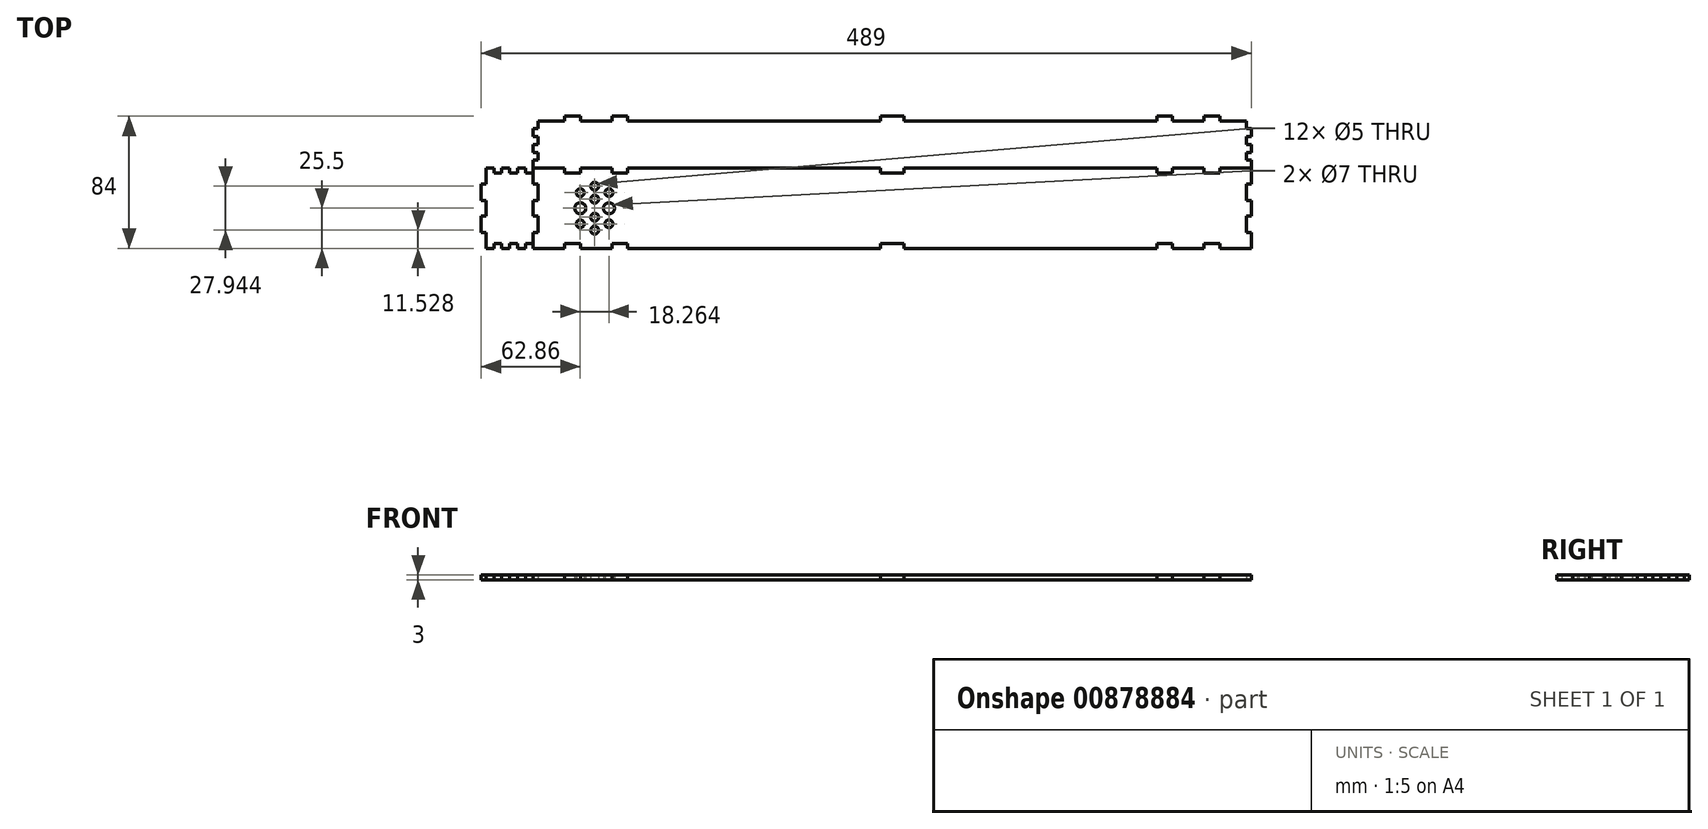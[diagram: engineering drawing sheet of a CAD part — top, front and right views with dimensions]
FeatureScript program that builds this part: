
annotation { "Feature Type Name" : "Feature", "Feature Type Description" : "" }
export const myFeature = defineFeature(function(context is Context, id is Id, definition is map)
    precondition{}
    {
        {
            assignVariable(context, id + "F0", {"name" : "MDF", "anyValue" : 3});
        }
        {
            var Q0;
            Q0=qCreatedBy(makeId("Top.planeOp"),FACE);
            var sketch = newSketch(context, id + "F1", { "sketchPlane" : qUnion([Q0])});
            skLineSegment(sketch, "E0", {"start": v(-228, 25.5) * mm, "end": v(-208, 25.5) * mm});
            skLineSegment(sketch, "E1", {"start": v(228, 25.5) * mm, "end": v(228, 15.5) * mm});
            skLineSegment(sketch, "E2", {"start": v(-228, -25.5) * mm, "end": v(-228, -15.5) * mm});
            skLineSegment(sketch, "E3", {"start": v(-198, 25.5) * mm, "end": v(-178, 25.5) * mm});
            skLineSegment(sketch, "E4", {"start": v(-208, 25.5) * mm, "end": v(-208, 22.5) * mm});
            skLineSegment(sketch, "E5", {"start": v(-208, 22.5) * mm, "end": v(-198, 22.5) * mm});
            skLineSegment(sketch, "E6", {"start": v(-198, 22.5) * mm, "end": v(-198, 25.5) * mm});
            skLineSegment(sketch, "E7.1.0.0", {"start": v(-178, 25.5) * mm, "end": v(-178, 22.5) * mm});
            skLineSegment(sketch, "E7.1.0.2", {"start": v(-168, 22.5) * mm, "end": v(-168, 25.5) * mm});
            skLineSegment(sketch, "E7.2.0.0", {"start": v(-7.5, 25.5) * mm, "end": v(-7.5, 22.5) * mm});
            skLineSegment(sketch, "E8.trimOffspring", {"start": v(-168, 25.5) * mm, "end": v(-7.5, 25.5) * mm});
            skLineSegment(sketch, "E9", {"start": v(-178, 22.5) * mm, "end": v(-168, 22.5) * mm});
            skLineSegment(sketch, "E10.MirrorCS", {"start": v(208, 25.5) * mm, "end": v(208, 22.5) * mm});
            skLineSegment(sketch, "E11.MirrorCS", {"start": v(198, 22.5) * mm, "end": v(198, 25.5) * mm});
            skLineSegment(sketch, "E12.MirrorCS", {"start": v(198, 25.5) * mm, "end": v(178, 25.5) * mm});
            skLineSegment(sketch, "E13.MirrorCS", {"start": v(178, 25.5) * mm, "end": v(178, 22.5) * mm});
            skLineSegment(sketch, "E14.MirrorCS", {"start": v(168, 22.5) * mm, "end": v(168, 25.5) * mm});
            skLineSegment(sketch, "E15.MirrorCS", {"start": v(168, 25.5) * mm, "end": v(7.5, 25.5) * mm});
            skLineSegment(sketch, "E16.MirrorCS", {"start": v(7.5, 25.5) * mm, "end": v(7.5, 22.5) * mm});
            skLineSegment(sketch, "E17", {"start": v(-7.5, 22.5) * mm, "end": v(7.5, 22.5) * mm});
            skLineSegment(sketch, "E18", {"start": v(168, 22.5) * mm, "end": v(178, 22.5) * mm});
            skLineSegment(sketch, "E19", {"start": v(198, 22.5) * mm, "end": v(208, 22.5) * mm});
            skLineSegment(sketch, "E20", {"start": v(-90, 40.5) * mm, "end": v(148.24, 40.5) * mm, "construction": true});
            skLineSegment(sketch, "E21", {"start": v(-228, 15.5) * mm, "end": v(-225, 15.5) * mm});
            skLineSegment(sketch, "E22", {"start": v(-225, 15.5) * mm, "end": v(-225, 5) * mm});
            skLineSegment(sketch, "E23", {"start": v(-225, -5) * mm, "end": v(-228, -5) * mm});
            skLineSegment(sketch, "E24.MirrorCS", {"start": v(-228, -15.5) * mm, "end": v(-225, -15.5) * mm});
            skLineSegment(sketch, "E25.MirrorCS", {"start": v(-225, -15.5) * mm, "end": v(-225, -5) * mm});
            skLineSegment(sketch, "E26.MirrorCS", {"start": v(-225, 5) * mm, "end": v(-228, 5) * mm});
            skLineSegment(sketch, "E27.trimOffspring", {"start": v(-228, -5) * mm, "end": v(-228, 5) * mm});
            skLineSegment(sketch, "E28.MirrorCS", {"start": v(225, -5) * mm, "end": v(228, -5) * mm});
            skLineSegment(sketch, "E29.MirrorCS", {"start": v(228, 15.5) * mm, "end": v(225, 15.5) * mm});
            skLineSegment(sketch, "E30.MirrorCS", {"start": v(225, 5) * mm, "end": v(228, 5) * mm});
            skLineSegment(sketch, "E31.MirrorCS", {"start": v(228, -15.5) * mm, "end": v(225, -15.5) * mm});
            skLineSegment(sketch, "E32.trimOffspring", {"start": v(228, 5) * mm, "end": v(228, -5) * mm});
            skLineSegment(sketch, "E33.trimOffspring", {"start": v(228, -15.5) * mm, "end": v(228, -25.5) * mm});
            skLineSegment(sketch, "E34.MirrorCS", {"start": v(-208, -22.5) * mm, "end": v(-198, -22.5) * mm});
            skLineSegment(sketch, "E35.MirrorCS", {"start": v(-178, -22.5) * mm, "end": v(-168, -22.5) * mm});
            skLineSegment(sketch, "E36.MirrorCS", {"start": v(-7.5, -22.5) * mm, "end": v(7.5, -22.5) * mm});
            skLineSegment(sketch, "E37.MirrorCS", {"start": v(168, -22.5) * mm, "end": v(178, -22.5) * mm});
            skLineSegment(sketch, "E38.MirrorCS", {"start": v(198, -22.5) * mm, "end": v(208, -22.5) * mm});
            skLineSegment(sketch, "E39.MirrorCS", {"start": v(-208, -25.5) * mm, "end": v(-208, -22.5) * mm});
            skLineSegment(sketch, "E40.MirrorCS", {"start": v(-198, -22.5) * mm, "end": v(-198, -25.5) * mm});
            skLineSegment(sketch, "E41.MirrorCS", {"start": v(-178, -25.5) * mm, "end": v(-178, -22.5) * mm});
            skLineSegment(sketch, "E42.MirrorCS", {"start": v(-168, -22.5) * mm, "end": v(-168, -25.5) * mm});
            skLineSegment(sketch, "E43.MirrorCS", {"start": v(-7.5, -25.5) * mm, "end": v(-7.5, -22.5) * mm});
            skLineSegment(sketch, "E44.MirrorCS", {"start": v(7.5, -25.5) * mm, "end": v(7.5, -22.5) * mm});
            skLineSegment(sketch, "E45.MirrorCS", {"start": v(168, -22.5) * mm, "end": v(168, -25.5) * mm});
            skLineSegment(sketch, "E46.MirrorCS", {"start": v(178, -25.5) * mm, "end": v(178, -22.5) * mm});
            skLineSegment(sketch, "E47.MirrorCS", {"start": v(198, -22.5) * mm, "end": v(198, -25.5) * mm});
            skLineSegment(sketch, "E48.MirrorCS", {"start": v(208, -25.5) * mm, "end": v(208, -22.5) * mm});
            skLineSegment(sketch, "E49.trimOffspring", {"start": v(-208, -25.5) * mm, "end": v(-228, -25.5) * mm});
            skLineSegment(sketch, "E50.trimOffspring", {"start": v(-178, -25.5) * mm, "end": v(-198, -25.5) * mm});
            skLineSegment(sketch, "E51.trimOffspring", {"start": v(-7.5, -25.5) * mm, "end": v(-168, -25.5) * mm});
            skLineSegment(sketch, "E52.trimOffspring", {"start": v(168, -25.5) * mm, "end": v(7.5, -25.5) * mm});
            skLineSegment(sketch, "E53.trimOffspring", {"start": v(198, -25.5) * mm, "end": v(178, -25.5) * mm});
            skLineSegment(sketch, "E54", {"start": v(208, 25.5) * mm, "end": v(228, 25.5) * mm});
            skLineSegment(sketch, "E55", {"start": v(-228, 15.5) * mm, "end": v(-228, 25.5) * mm});
            skLineSegment(sketch, "E56", {"start": v(208, -25.5) * mm, "end": v(228, -25.5) * mm});
            skLineSegment(sketch, "E57", {"start": v(-228, 25.5) * mm, "end": v(-307.39, 109.63) * mm, "construction": true});
            skLineSegment(sketch, "E58", {"start": v(-228, 25.5) * mm, "end": v(-74.23, 179.27) * mm, "construction": true});
            skLineSegment(sketch, "E59.MirrorCS", {"start": v(-228, 25.5) * mm, "end": v(-228, 30.5) * mm});
            skLineSegment(sketch, "E60.MirrorCS", {"start": v(-225, 55.5) * mm, "end": v(-208, 55.5) * mm});
            skLineSegment(sketch, "E61.MirrorCS", {"start": v(-208, 55.5) * mm, "end": v(-208, 58.5) * mm});
            skLineSegment(sketch, "E62.MirrorCS", {"start": v(-208, 58.5) * mm, "end": v(-198, 58.5) * mm});
            skLineSegment(sketch, "E63.MirrorCS", {"start": v(-198, 58.5) * mm, "end": v(-198, 55.5) * mm});
            skLineSegment(sketch, "E64.MirrorCS", {"start": v(-198, 55.5) * mm, "end": v(-178, 55.5) * mm});
            skLineSegment(sketch, "E65.MirrorCS", {"start": v(-178, 55.5) * mm, "end": v(-178, 58.5) * mm});
            skLineSegment(sketch, "E66.MirrorCS", {"start": v(-178, 58.5) * mm, "end": v(-168, 58.5) * mm});
            skLineSegment(sketch, "E67.MirrorCS", {"start": v(-168, 58.5) * mm, "end": v(-168, 55.5) * mm});
            skLineSegment(sketch, "E68.MirrorCS", {"start": v(-168, 55.5) * mm, "end": v(-7.5, 55.5) * mm});
            skLineSegment(sketch, "E69.MirrorCS", {"start": v(-7.5, 55.5) * mm, "end": v(-7.5, 58.5) * mm});
            skLineSegment(sketch, "E70.MirrorCS", {"start": v(-7.5, 58.5) * mm, "end": v(7.5, 58.5) * mm});
            skLineSegment(sketch, "E71.MirrorCS", {"start": v(7.5, 55.5) * mm, "end": v(7.5, 58.5) * mm});
            skLineSegment(sketch, "E72.MirrorCS", {"start": v(168, 55.5) * mm, "end": v(7.5, 55.5) * mm});
            skLineSegment(sketch, "E73.MirrorCS", {"start": v(168, 58.5) * mm, "end": v(168, 55.5) * mm});
            skLineSegment(sketch, "E74.MirrorCS", {"start": v(168, 58.5) * mm, "end": v(178, 58.5) * mm});
            skLineSegment(sketch, "E75.MirrorCS", {"start": v(178, 55.5) * mm, "end": v(178, 58.5) * mm});
            skLineSegment(sketch, "E76.MirrorCS", {"start": v(198, 55.5) * mm, "end": v(178, 55.5) * mm});
            skLineSegment(sketch, "E77.MirrorCS", {"start": v(198, 58.5) * mm, "end": v(198, 55.5) * mm});
            skLineSegment(sketch, "E78.MirrorCS", {"start": v(198, 58.5) * mm, "end": v(208, 58.5) * mm});
            skLineSegment(sketch, "E79.MirrorCS", {"start": v(208, 55.5) * mm, "end": v(208, 58.5) * mm});
            skLineSegment(sketch, "E80.MirrorCS", {"start": v(208, 55.5) * mm, "end": v(228, 55.5) * mm});
            skLineSegment(sketch, "E81.MirrorCS", {"start": v(228, -111.4) * mm, "end": v(225, -111.4) * mm});
            skLineSegment(sketch, "E82.MirrorCS", {"start": v(225, -121.4) * mm, "end": v(225, -111.4) * mm});
            skLineSegment(sketch, "E83.MirrorCS", {"start": v(228, -121.4) * mm, "end": v(225, -121.4) * mm});
            skLineSegment(sketch, "E84.MirrorCS", {"start": v(228, -142.55) * mm, "end": v(228, -121.4) * mm});
            skLineSegment(sketch, "E85.MirrorCS", {"start": v(228, -142.55) * mm, "end": v(225, -142.55) * mm});
            skLineSegment(sketch, "E86", {"start": v(228, 50.5) * mm, "end": v(228, 45.5) * mm});
            skPoint(sketch, "E87.orphan", {"position": v(-228, 147.7) * mm});
            skLineSegment(sketch, "E88", {"start": v(65.44, -22.5) * mm, "end": v(-228, -22.5) * mm, "construction": true});
            skLineSegment(sketch, "E89", {"start": v(225, 15.5) * mm, "end": v(225, 5) * mm});
            skLineSegment(sketch, "E90", {"start": v(225, -5) * mm, "end": v(225, -15.5) * mm});
            skLineSegment(sketch, "E91", {"start": v(-228, 22.5) * mm, "end": v(-233, 22.5) * mm});
            skLineSegment(sketch, "E92", {"start": v(-233, 22.5) * mm, "end": v(-233, 25.5) * mm});
            skLineSegment(sketch, "E93", {"start": v(-233, 25.5) * mm, "end": v(-238, 25.5) * mm});
            skLineSegment(sketch, "E94", {"start": v(-238, 25.5) * mm, "end": v(-238, 22.5) * mm});
            skLineSegment(sketch, "E95", {"start": v(-238, 22.5) * mm, "end": v(-243, 22.5) * mm});
            skLineSegment(sketch, "E96", {"start": v(-243, 22.5) * mm, "end": v(-243, 25.5) * mm});
            skLineSegment(sketch, "E97", {"start": v(-243, 25.5) * mm, "end": v(-248, 25.5) * mm});
            skLineSegment(sketch, "E98", {"start": v(-248, 25.5) * mm, "end": v(-248, 22.5) * mm});
            skPoint(sketch, "E98.endSnap0", {"position": v(-240.5, 22.5) * mm});
            skLineSegment(sketch, "E99", {"start": v(-248, 22.5) * mm, "end": v(-253, 22.5) * mm});
            skLineSegment(sketch, "E100", {"start": v(-253, 22.5) * mm, "end": v(-253, 25.5) * mm});
            skLineSegment(sketch, "E101", {"start": v(-253, 25.5) * mm, "end": v(-258, 25.5) * mm});
            skLineSegment(sketch, "E102", {"start": v(-258, 25.5) * mm, "end": v(-258, 15.5) * mm});
            skLineSegment(sketch, "E103", {"start": v(-255.3, 0) * mm, "end": v(-174.46, 0) * mm, "construction": true});
            skLineSegment(sketch, "E104.MirrorCS", {"start": v(-258, -25.5) * mm, "end": v(-258, -15.5) * mm});
            skLineSegment(sketch, "E105.MirrorCS", {"start": v(-253, -25.5) * mm, "end": v(-258, -25.5) * mm});
            skLineSegment(sketch, "E106.MirrorCS", {"start": v(-253, -22.5) * mm, "end": v(-253, -25.5) * mm});
            skLineSegment(sketch, "E107.MirrorCS", {"start": v(-248, -22.5) * mm, "end": v(-253, -22.5) * mm});
            skLineSegment(sketch, "E108.MirrorCS", {"start": v(-248, -25.5) * mm, "end": v(-248, -22.5) * mm});
            skLineSegment(sketch, "E109.MirrorCS", {"start": v(-243, -25.5) * mm, "end": v(-248, -25.5) * mm});
            skLineSegment(sketch, "E110.MirrorCS", {"start": v(-243, -22.5) * mm, "end": v(-243, -25.5) * mm});
            skLineSegment(sketch, "E111.MirrorCS", {"start": v(-238, -22.5) * mm, "end": v(-243, -22.5) * mm});
            skLineSegment(sketch, "E112.MirrorCS", {"start": v(-238, -25.5) * mm, "end": v(-238, -22.5) * mm});
            skLineSegment(sketch, "E113.MirrorCS", {"start": v(-233, -25.5) * mm, "end": v(-238, -25.5) * mm});
            skLineSegment(sketch, "E114.MirrorCS", {"start": v(-233, -22.5) * mm, "end": v(-233, -25.5) * mm});
            skLineSegment(sketch, "E115.MirrorCS", {"start": v(-228, -22.5) * mm, "end": v(-233, -22.5) * mm});
            skLineSegment(sketch, "E116", {"start": v(-258, 15.5) * mm, "end": v(-261, 15.5) * mm});
            skLineSegment(sketch, "E117", {"start": v(-261, 15.5) * mm, "end": v(-261, 5) * mm});
            skLineSegment(sketch, "E118", {"start": v(-261, 5) * mm, "end": v(-258, 5) * mm});
            skLineSegment(sketch, "E119", {"start": v(-258, 5) * mm, "end": v(-258, -5) * mm});
            skLineSegment(sketch, "E120", {"start": v(-258, -5) * mm, "end": v(-261, -5) * mm});
            skLineSegment(sketch, "E121", {"start": v(-261, -5) * mm, "end": v(-261, -15.5) * mm});
            skLineSegment(sketch, "E122", {"start": v(-261, -15.5) * mm, "end": v(-258, -15.5) * mm});
            skLineSegment(sketch, "E123.trimOffspring", {"start": v(-258, 5) * mm, "end": v(-258, 0) * mm});
            skLineSegment(sketch, "E124.trimOffspring", {"start": v(-258, -5) * mm, "end": v(-258, 0) * mm});
            skLineSegment(sketch, "E125", {"start": v(-228, 30.5) * mm, "end": v(-225, 30.5) * mm});
            skLineSegment(sketch, "E126", {"start": v(-225, 30.5) * mm, "end": v(-225, 35.5) * mm});
            skLineSegment(sketch, "E127", {"start": v(-225, 35.5) * mm, "end": v(-228, 35.5) * mm});
            skLineSegment(sketch, "E128", {"start": v(-228, 40.5) * mm, "end": v(-225, 40.5) * mm});
            skLineSegment(sketch, "E129", {"start": v(-225, 40.5) * mm, "end": v(-225, 45.5) * mm});
            skLineSegment(sketch, "E130", {"start": v(-225, 45.5) * mm, "end": v(-228, 45.5) * mm});
            skLineSegment(sketch, "E131", {"start": v(-225, 50.5) * mm, "end": v(-225, 55.5) * mm});
            skLineSegment(sketch, "E132.trimOffspring", {"start": v(-228, 35.5) * mm, "end": v(-228, 40.5) * mm});
            skLineSegment(sketch, "E133.trimOffspring", {"start": v(-228, 45.5) * mm, "end": v(-228, 50.5) * mm});
            skLineSegment(sketch, "E134", {"start": v(-228, 50.5) * mm, "end": v(-225, 50.5) * mm});
            skLineSegment(sketch, "E135", {"start": v(0, 0) * mm, "end": v(0, 93.3) * mm, "construction": true});
            skLineSegment(sketch, "E136.MirrorCS", {"start": v(225, 50.5) * mm, "end": v(225, 55.5) * mm});
            skLineSegment(sketch, "E137.MirrorCS", {"start": v(228, 50.5) * mm, "end": v(225, 50.5) * mm});
            skLineSegment(sketch, "E138.MirrorCS", {"start": v(228, 45.5) * mm, "end": v(228, 50.5) * mm});
            skLineSegment(sketch, "E139.MirrorCS", {"start": v(225, 45.5) * mm, "end": v(228, 45.5) * mm});
            skLineSegment(sketch, "E140.MirrorCS", {"start": v(225, 40.5) * mm, "end": v(225, 45.5) * mm});
            skLineSegment(sketch, "E141.MirrorCS", {"start": v(228, 40.5) * mm, "end": v(225, 40.5) * mm});
            skLineSegment(sketch, "E142.MirrorCS", {"start": v(228, 35.5) * mm, "end": v(228, 40.5) * mm});
            skLineSegment(sketch, "E143.MirrorCS", {"start": v(225, 35.5) * mm, "end": v(228, 35.5) * mm});
            skLineSegment(sketch, "E144.MirrorCS", {"start": v(225, 30.5) * mm, "end": v(225, 35.5) * mm});
            skLineSegment(sketch, "E145.MirrorCS", {"start": v(228, 30.5) * mm, "end": v(225, 30.5) * mm});
            skLineSegment(sketch, "E146.MirrorCS", {"start": v(228, 25.5) * mm, "end": v(228, 30.5) * mm});
            skLineSegment(sketch, "E147.trimOffspring", {"start": v(228, 30.5) * mm, "end": v(228, 25.5) * mm});
            skLineSegment(sketch, "E148.trimOffspring", {"start": v(228, 40.5) * mm, "end": v(228, 35.5) * mm});
            skCircle(sketch, "E149", {"center": v(-198.14, 9.9) * mm, "radius": 2.5 * mm});
            skCircle(sketch, "E150", {"center": v(-189.01, 13.97) * mm, "radius": 2.5 * mm});
            skCircle(sketch, "E151", {"center": v(-179.88, 9.9) * mm, "radius": 2.5 * mm});
            skCircle(sketch, "E152", {"center": v(-189.01, 5.7) * mm, "radius": 2.5 * mm});
            skCircle(sketch, "E153.MirrorC", {"center": v(-179.88, -9.9) * mm, "radius": 2.5 * mm});
            skCircle(sketch, "E154.MirrorC", {"center": v(-189.01, -5.7) * mm, "radius": 2.5 * mm});
            skCircle(sketch, "E155.MirrorC", {"center": v(-189.01, -13.97) * mm, "radius": 2.5 * mm});
            skCircle(sketch, "E156.MirrorC", {"center": v(-198.14, -9.9) * mm, "radius": 2.5 * mm});
            skCircle(sketch, "E157", {"center": v(-198.14, 0) * mm, "radius": 3.5 * mm});
            skCircle(sketch, "E158", {"center": v(-179.88, 0) * mm, "radius": 3.5 * mm});
            skSolve(sketch);
        }
        {
            var Q0;
            {var subQ4=sQuery(id+"F1.wireOp",EDGE,"E21");Q0=makeQuery(id+"F1.imprint","IMPRINT",FACE,{"disambiguationData":[TD([[makeQuery(id+"F1.imprint","IMPRINT",EDGE,{"derivedFrom":subQ4}),-1.0]])]});}
            var Q1;
            {var subQ0=sQuery(id+"F1.wireOp",EDGE,"rbGXvyEr-rcJ9-qHWQ-iufH-F8PwVDv6k9id");Q1=makeQuery(id+"F1.imprint","IMPRINT",FACE,{"disambiguationData":[TD([[makeQuery(id+"F1.imprint","IMPRINT",EDGE,{"derivedFrom":subQ0}),-1.0]])]});}
            var Q2;
            {var subQ4=sQuery(id+"F1.wireOp",EDGE,"E21");Q2=makeQuery(id+"F1.imprint","IMPRINT",FACE,{"disambiguationData":[TD([[makeQuery(id+"F1.imprint","IMPRINT",EDGE,{"derivedFrom":subQ4}),-1.0]])]});}
            var Q3;
            {var subQ0=sQuery(id+"F1.wireOp",EDGE,"GfZ24xhA-2xWa-IL8O-etRM-yisPiMKkurjO");Q3=makeQuery(id+"F1.imprint","IMPRINT",FACE,{"disambiguationData":[TD([[makeQuery(id+"F1.imprint","IMPRINT",EDGE,{"derivedFrom":subQ0}),-1.0]])]});}
            extrude(context, id + "F2", {"entities" : qUnion([Q0, Q1, Q2, Q3]), "depth" : (getVariable(context, 'MDF')) * mm, "offsetDistance" : 25 * mm});
        }
        {
            var Q0;
            {var subQ2=sQuery(id+"F1.wireOp",EDGE,"E0");Q0=makeQuery(id+"F1.imprint","IMPRINT",FACE,{"disambiguationData":[TD([[makeQuery(id+"F1.imprint","IMPRINT",EDGE,{"derivedFrom":subQ2}),-1.0]])]});}
            var Q1;
            {var subQ0=sQuery(id+"F1.wireOp",EDGE,"rbGXvyEr-rcJ9-qHWQ-iufH-F8PwVDv6k9id");Q1=makeQuery(id+"F1.imprint","IMPRINT",FACE,{"disambiguationData":[TD([[makeQuery(id+"F1.imprint","IMPRINT",EDGE,{"derivedFrom":subQ0}),-1.0]])]});}
            var Q2;
            {var subQ0=sQuery(id+"F1.wireOp",EDGE,"YcIgSpRp-awep-ehTJ-AOBv-wXQJOqJfKg8G");Q2=makeQuery(id+"F1.imprint","IMPRINT",FACE,{"disambiguationData":[TD([[makeQuery(id+"F1.imprint","IMPRINT",EDGE,{"derivedFrom":subQ0}),-1.0]])]});}
            var Q3;
            {var subQ4=sQuery(id+"F1.wireOp",EDGE,"E21");Q3=makeQuery(id+"F1.imprint","IMPRINT",FACE,{"disambiguationData":[TD([[makeQuery(id+"F1.imprint","IMPRINT",EDGE,{"derivedFrom":subQ4}),-1.0]])]});}
            var Q4;
            {var subQ0=sQuery(id+"F1.wireOp",EDGE,"GfZ24xhA-2xWa-IL8O-etRM-yisPiMKkurjO");Q4=makeQuery(id+"F1.imprint","IMPRINT",FACE,{"disambiguationData":[TD([[makeQuery(id+"F1.imprint","IMPRINT",EDGE,{"derivedFrom":subQ0}),-1.0]])]});}
            var Q5;
            {var subQ0=sQuery(id+"F1.wireOp",EDGE,"T6HoQtfU-LjOd-NWtG-YFmk-kXrqQ6T8l042");Q5=makeQuery(id+"F1.imprint","IMPRINT",FACE,{"disambiguationData":[TD([[makeQuery(id+"F1.imprint","IMPRINT",EDGE,{"derivedFrom":subQ0}),-1.0]])]});}
            var Q6;
            Q6=makeQuery(id+"F1.imprint","IMPRINT",FACE,{"disambiguationData":[TD([[makeQuery(id+"F1.imprint","IMPRINT",EDGE,{"derivedFrom":sQuery(id+"F1.wireOp",EDGE,"E1")}),1.0]])]});
            var Q7;
            Q7=makeQuery(id+"F1.imprint","IMPRINT",FACE,{"disambiguationData":[TD([[makeQuery(id+"F1.imprint","IMPRINT",EDGE,{"derivedFrom":sQuery(id+"F1.wireOp",EDGE,"E32.trimOffspring")}),1.0]])]});
            var Q8;
            {var subQ1=sQuery(id+"F1.wireOp",EDGE,"E33.trimOffspring");Q8=makeQuery(id+"F1.imprint","IMPRINT",FACE,{"disambiguationData":[TD([[makeQuery(id+"F1.imprint","IMPRINT",EDGE,{"derivedFrom":subQ1}),1.0]])]});}
            var Q9;
            Q9=makeQuery(id+"F1.imprint","IMPRINT",FACE,{"disambiguationData":[TD([[makeQuery(id+"F1.imprint","IMPRINT",EDGE,{"derivedFrom":sQuery(id+"F1.wireOp",EDGE,"NR7x9NeR-g1uV-OuWE-nqgm-Qy7388QoDPan")}),1.0]])]});
            var Q10;
            Q10=makeQuery(id+"F1.imprint","IMPRINT",FACE,{"disambiguationData":[TD([[makeQuery(id+"F1.imprint","IMPRINT",EDGE,{"derivedFrom":sQuery(id+"F1.wireOp",EDGE,"OMaXj8xA-5qEw-IC3M-FVCK-IZFmudWBQMBu")}),1.0]])]});
            extrude(context, id + "F3", {"entities" : qUnion([Q0, Q1, Q2, Q3, Q4, Q5, Q6, Q7, Q8, Q9, Q10]), "depth" : (getVariable(context, 'MDF')) * mm, "offsetDistance" : 25 * mm});
        }
        {
            var Q0;
            {var subQ2=sQuery(id+"F1.wireOp",EDGE,"E0");Q0=makeQuery(id+"F1.imprint","IMPRINT",FACE,{"disambiguationData":[TD([[makeQuery(id+"F1.imprint","IMPRINT",EDGE,{"derivedFrom":subQ2}),-1.0]])]});}
            extrude(context, id + "F4", {"entities" : qUnion([Q0]), "depth" : (getVariable(context, 'MDF')) * mm, "offsetDistance" : 25 * mm});
        }
        {
            var Q0;
            Q0=makeQuery(id+"F1.imprint","IMPRINT",FACE,{"disambiguationData":[TD([[makeQuery(id+"F1.imprint","IMPRINT",EDGE,{"derivedFrom":sQuery(id+"F1.wireOp",EDGE,"E0")}),1.0]])]});
            extrude(context, id + "F5", {"entities" : qUnion([Q0]), "depth" : (getVariable(context, 'MDF')) * mm, "offsetDistance" : 25 * mm});
        }
        {
            var Q0;
            {var subQ4=sQuery(id+"F1.wireOp",EDGE,"E21");Q0=makeQuery(id+"F1.imprint","IMPRINT",FACE,{"disambiguationData":[TD([[makeQuery(id+"F1.imprint","IMPRINT",EDGE,{"derivedFrom":subQ4}),-1.0]])]});}
            extrude(context, id + "F6", {"entities" : qUnion([Q0]), "depth" : (getVariable(context, 'MDF')) * mm, "offsetDistance" : 25 * mm});
        }
        {
            var Q0;
            Q0=makeQuery(id+"F2.opExtrude","SWEPT_BODY",BODY,{"disambiguationData":[OSD([sQuery(id+"F1.wireOp",EDGE,"E2"),sQuery(id+"F1.wireOp",EDGE,"E21"),sQuery(id+"F1.wireOp",EDGE,"E22"),sQuery(id+"F1.wireOp",EDGE,"E23"),sQuery(id+"F1.wireOp",EDGE,"E24.MirrorCS"),sQuery(id+"F1.wireOp",EDGE,"E25.MirrorCS"),sQuery(id+"F1.wireOp",EDGE,"E26.MirrorCS"),sQuery(id+"F1.wireOp",EDGE,"E27.trimOffspring"),sQuery(id+"F1.wireOp",EDGE,"E55"),sQuery(id+"F1.wireOp",EDGE,"E91"),sQuery(id+"F1.wireOp",EDGE,"E92"),sQuery(id+"F1.wireOp",EDGE,"E93"),sQuery(id+"F1.wireOp",EDGE,"E94"),sQuery(id+"F1.wireOp",EDGE,"E95"),sQuery(id+"F1.wireOp",EDGE,"E96"),sQuery(id+"F1.wireOp",EDGE,"E97"),sQuery(id+"F1.wireOp",EDGE,"E98"),sQuery(id+"F1.wireOp",EDGE,"E99"),sQuery(id+"F1.wireOp",EDGE,"E100"),sQuery(id+"F1.wireOp",EDGE,"E101"),sQuery(id+"F1.wireOp",EDGE,"E102"),sQuery(id+"F1.wireOp",EDGE,"E104.MirrorCS"),sQuery(id+"F1.wireOp",EDGE,"E105.MirrorCS"),sQuery(id+"F1.wireOp",EDGE,"E106.MirrorCS"),sQuery(id+"F1.wireOp",EDGE,"E107.MirrorCS"),sQuery(id+"F1.wireOp",EDGE,"E108.MirrorCS"),sQuery(id+"F1.wireOp",EDGE,"E109.MirrorCS"),sQuery(id+"F1.wireOp",EDGE,"E110.MirrorCS"),sQuery(id+"F1.wireOp",EDGE,"E111.MirrorCS"),sQuery(id+"F1.wireOp",EDGE,"E112.MirrorCS"),sQuery(id+"F1.wireOp",EDGE,"E113.MirrorCS"),sQuery(id+"F1.wireOp",EDGE,"E114.MirrorCS"),sQuery(id+"F1.wireOp",EDGE,"E115.MirrorCS"),sQuery(id+"F1.wireOp",EDGE,"E116"),sQuery(id+"F1.wireOp",EDGE,"E117"),sQuery(id+"F1.wireOp",EDGE,"E118"),sQuery(id+"F1.wireOp",EDGE,"E119"),sQuery(id+"F1.wireOp",EDGE,"E120"),sQuery(id+"F1.wireOp",EDGE,"E121"),sQuery(id+"F1.wireOp",EDGE,"E122")])]});
            deleteBodies(context, id + "F7", {"entities" : qUnion([Q0])});
        }
        {
            var Q0;
            Q0=makeQuery(id+"F3.opExtrude","SWEPT_BODY",BODY,{"disambiguationData":[OSD([sQuery(id+"F1.wireOp",EDGE,"E0"),sQuery(id+"F1.wireOp",EDGE,"E1"),sQuery(id+"F1.wireOp",EDGE,"E2"),sQuery(id+"F1.wireOp",EDGE,"E3"),sQuery(id+"F1.wireOp",EDGE,"E4"),sQuery(id+"F1.wireOp",EDGE,"E5"),sQuery(id+"F1.wireOp",EDGE,"E6"),sQuery(id+"F1.wireOp",EDGE,"E7.1.0.0"),sQuery(id+"F1.wireOp",EDGE,"E7.1.0.2"),sQuery(id+"F1.wireOp",EDGE,"E7.2.0.0"),sQuery(id+"F1.wireOp",EDGE,"E8.trimOffspring"),sQuery(id+"F1.wireOp",EDGE,"E9"),sQuery(id+"F1.wireOp",EDGE,"E10.MirrorCS"),sQuery(id+"F1.wireOp",EDGE,"E11.MirrorCS"),sQuery(id+"F1.wireOp",EDGE,"E12.MirrorCS"),sQuery(id+"F1.wireOp",EDGE,"E13.MirrorCS"),sQuery(id+"F1.wireOp",EDGE,"E14.MirrorCS"),sQuery(id+"F1.wireOp",EDGE,"E15.MirrorCS"),sQuery(id+"F1.wireOp",EDGE,"E16.MirrorCS"),sQuery(id+"F1.wireOp",EDGE,"E17"),sQuery(id+"F1.wireOp",EDGE,"E18"),sQuery(id+"F1.wireOp",EDGE,"E19"),sQuery(id+"F1.wireOp",EDGE,"E28.MirrorCS"),sQuery(id+"F1.wireOp",EDGE,"E29.MirrorCS"),sQuery(id+"F1.wireOp",EDGE,"E30.MirrorCS"),sQuery(id+"F1.wireOp",EDGE,"E31.MirrorCS"),sQuery(id+"F1.wireOp",EDGE,"E32.trimOffspring"),sQuery(id+"F1.wireOp",EDGE,"E33.trimOffspring"),sQuery(id+"F1.wireOp",EDGE,"E34.MirrorCS"),sQuery(id+"F1.wireOp",EDGE,"E35.MirrorCS"),sQuery(id+"F1.wireOp",EDGE,"E36.MirrorCS"),sQuery(id+"F1.wireOp",EDGE,"E37.MirrorCS"),sQuery(id+"F1.wireOp",EDGE,"E38.MirrorCS"),sQuery(id+"F1.wireOp",EDGE,"E39.MirrorCS"),sQuery(id+"F1.wireOp",EDGE,"E40.MirrorCS"),sQuery(id+"F1.wireOp",EDGE,"E41.MirrorCS"),sQuery(id+"F1.wireOp",EDGE,"E42.MirrorCS"),sQuery(id+"F1.wireOp",EDGE,"E43.MirrorCS"),sQuery(id+"F1.wireOp",EDGE,"E44.MirrorCS"),sQuery(id+"F1.wireOp",EDGE,"E45.MirrorCS"),sQuery(id+"F1.wireOp",EDGE,"E46.MirrorCS"),sQuery(id+"F1.wireOp",EDGE,"E47.MirrorCS"),sQuery(id+"F1.wireOp",EDGE,"E48.MirrorCS"),sQuery(id+"F1.wireOp",EDGE,"E49.trimOffspring"),sQuery(id+"F1.wireOp",EDGE,"E50.trimOffspring"),sQuery(id+"F1.wireOp",EDGE,"E51.trimOffspring"),sQuery(id+"F1.wireOp",EDGE,"E52.trimOffspring"),sQuery(id+"F1.wireOp",EDGE,"E53.trimOffspring"),sQuery(id+"F1.wireOp",EDGE,"E54"),sQuery(id+"F1.wireOp",EDGE,"E55"),sQuery(id+"F1.wireOp",EDGE,"E56"),sQuery(id+"F1.wireOp",EDGE,"E89"),sQuery(id+"F1.wireOp",EDGE,"E90"),sQuery(id+"F1.wireOp",EDGE,"E91"),sQuery(id+"F1.wireOp",EDGE,"E92"),sQuery(id+"F1.wireOp",EDGE,"E93"),sQuery(id+"F1.wireOp",EDGE,"E94"),sQuery(id+"F1.wireOp",EDGE,"E95"),sQuery(id+"F1.wireOp",EDGE,"E96"),sQuery(id+"F1.wireOp",EDGE,"E97"),sQuery(id+"F1.wireOp",EDGE,"E98"),sQuery(id+"F1.wireOp",EDGE,"E99"),sQuery(id+"F1.wireOp",EDGE,"E100"),sQuery(id+"F1.wireOp",EDGE,"E101"),sQuery(id+"F1.wireOp",EDGE,"E102"),sQuery(id+"F1.wireOp",EDGE,"E104.MirrorCS"),sQuery(id+"F1.wireOp",EDGE,"E105.MirrorCS"),sQuery(id+"F1.wireOp",EDGE,"E106.MirrorCS"),sQuery(id+"F1.wireOp",EDGE,"E107.MirrorCS"),sQuery(id+"F1.wireOp",EDGE,"E108.MirrorCS"),sQuery(id+"F1.wireOp",EDGE,"E109.MirrorCS"),sQuery(id+"F1.wireOp",EDGE,"E110.MirrorCS"),sQuery(id+"F1.wireOp",EDGE,"E111.MirrorCS"),sQuery(id+"F1.wireOp",EDGE,"E112.MirrorCS"),sQuery(id+"F1.wireOp",EDGE,"E113.MirrorCS"),sQuery(id+"F1.wireOp",EDGE,"E114.MirrorCS"),sQuery(id+"F1.wireOp",EDGE,"E115.MirrorCS"),sQuery(id+"F1.wireOp",EDGE,"E116"),sQuery(id+"F1.wireOp",EDGE,"E117"),sQuery(id+"F1.wireOp",EDGE,"E118"),sQuery(id+"F1.wireOp",EDGE,"E119"),sQuery(id+"F1.wireOp",EDGE,"E120"),sQuery(id+"F1.wireOp",EDGE,"E121"),sQuery(id+"F1.wireOp",EDGE,"E122"),sQuery(id+"F1.wireOp",EDGE,"E149"),sQuery(id+"F1.wireOp",EDGE,"E150"),sQuery(id+"F1.wireOp",EDGE,"E151"),sQuery(id+"F1.wireOp",EDGE,"E152"),sQuery(id+"F1.wireOp",EDGE,"E153.MirrorC"),sQuery(id+"F1.wireOp",EDGE,"E154.MirrorC"),sQuery(id+"F1.wireOp",EDGE,"E155.MirrorC"),sQuery(id+"F1.wireOp",EDGE,"E156.MirrorC"),sQuery(id+"F1.wireOp",EDGE,"E157"),sQuery(id+"F1.wireOp",EDGE,"E158")])]});
            deleteBodies(context, id + "F8", {"entities" : qUnion([Q0])});
        }
        {
            var Q0;
            {var subQ2=sQuery(id+"F1.wireOp",EDGE,"E0");Q0=makeQuery(id+"F1.imprint","IMPRINT",FACE,{"disambiguationData":[TD([[makeQuery(id+"F1.imprint","IMPRINT",EDGE,{"derivedFrom":subQ2}),-1.0]])]});}
            var Q1;
            Q1=makeQuery(id+"F1.imprint","IMPRINT",FACE,{"disambiguationData":[TD([[makeQuery(id+"F1.imprint","IMPRINT",EDGE,{"derivedFrom":sQuery(id+"F1.wireOp",EDGE,"E153.MirrorC")}),-1.0]])]});
            var Q2;
            Q2=makeQuery(id+"F1.imprint","IMPRINT",FACE,{"disambiguationData":[TD([[makeQuery(id+"F1.imprint","IMPRINT",EDGE,{"derivedFrom":sQuery(id+"F1.wireOp",EDGE,"E158")}),1.0]])]});
            var Q3;
            Q3=makeQuery(id+"F1.imprint","IMPRINT",FACE,{"disambiguationData":[TD([[makeQuery(id+"F1.imprint","IMPRINT",EDGE,{"derivedFrom":sQuery(id+"F1.wireOp",EDGE,"E151")}),1.0]])]});
            var Q4;
            Q4=makeQuery(id+"F1.imprint","IMPRINT",FACE,{"disambiguationData":[TD([[makeQuery(id+"F1.imprint","IMPRINT",EDGE,{"derivedFrom":sQuery(id+"F1.wireOp",EDGE,"E152")}),1.0]])]});
            var Q5;
            Q5=makeQuery(id+"F1.imprint","IMPRINT",FACE,{"disambiguationData":[TD([[makeQuery(id+"F1.imprint","IMPRINT",EDGE,{"derivedFrom":sQuery(id+"F1.wireOp",EDGE,"E154.MirrorC")}),-1.0]])]});
            var Q6;
            Q6=makeQuery(id+"F1.imprint","IMPRINT",FACE,{"disambiguationData":[TD([[makeQuery(id+"F1.imprint","IMPRINT",EDGE,{"derivedFrom":sQuery(id+"F1.wireOp",EDGE,"E155.MirrorC")}),-1.0]])]});
            var Q7;
            Q7=makeQuery(id+"F1.imprint","IMPRINT",FACE,{"disambiguationData":[TD([[makeQuery(id+"F1.imprint","IMPRINT",EDGE,{"derivedFrom":sQuery(id+"F1.wireOp",EDGE,"E156.MirrorC")}),-1.0]])]});
            var Q8;
            Q8=makeQuery(id+"F1.imprint","IMPRINT",FACE,{"disambiguationData":[TD([[makeQuery(id+"F1.imprint","IMPRINT",EDGE,{"derivedFrom":sQuery(id+"F1.wireOp",EDGE,"E157")}),1.0]])]});
            var Q9;
            Q9=makeQuery(id+"F1.imprint","IMPRINT",FACE,{"disambiguationData":[TD([[makeQuery(id+"F1.imprint","IMPRINT",EDGE,{"derivedFrom":sQuery(id+"F1.wireOp",EDGE,"E149")}),1.0]])]});
            var Q10;
            Q10=makeQuery(id+"F1.imprint","IMPRINT",FACE,{"disambiguationData":[TD([[makeQuery(id+"F1.imprint","IMPRINT",EDGE,{"derivedFrom":sQuery(id+"F1.wireOp",EDGE,"E150")}),1.0]])]});
            extrude(context, id + "F9", {"entities" : qUnion([Q0, Q1, Q2, Q3, Q4, Q5, Q6, Q7, Q8, Q9, Q10]), "depth" : (getVariable(context, 'MDF')) * mm, "offsetDistance" : 25 * mm});
        }
    });
